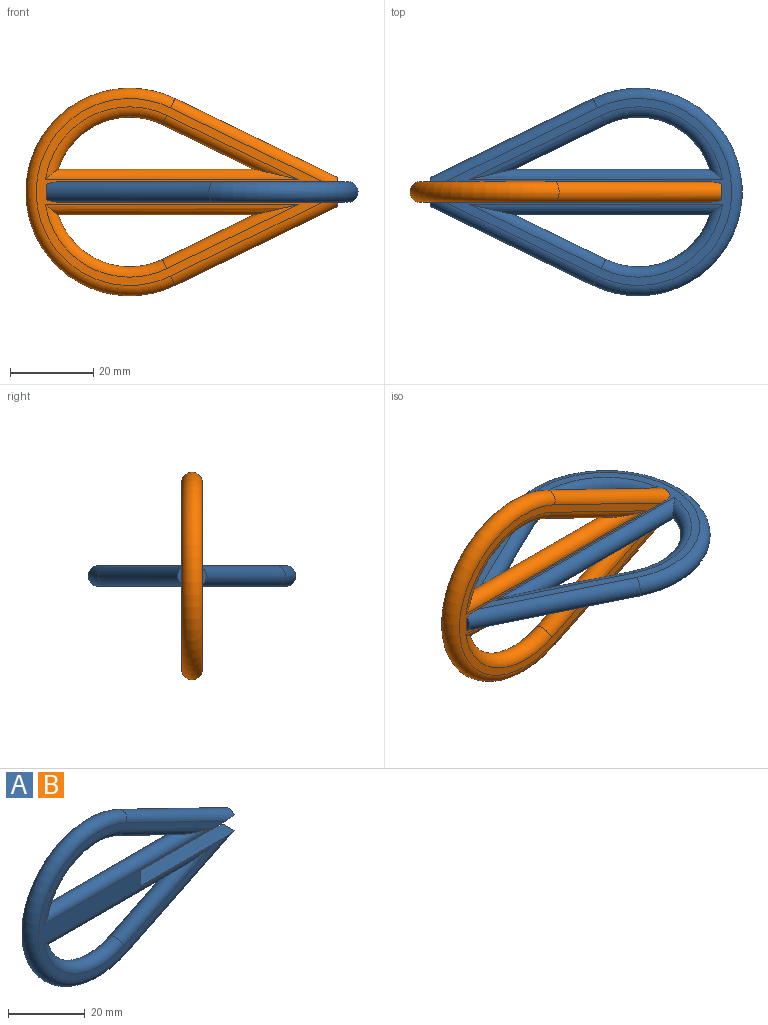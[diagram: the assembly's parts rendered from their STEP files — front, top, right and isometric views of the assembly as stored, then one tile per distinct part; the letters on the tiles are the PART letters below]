
ASSEMBLY  parts=2 mates=1
PART A: 16 faces, bbox 77.5x5x54.1 mm
  f0: plane 35x5mm, normal (0,0,-1), area 173.7mm2, adj f1,f4,f5,f6,f9
  f1: plane 3.84x1mm, normal (1,0,0), area 2.7mm2, adj f0,f9
  f2: plane 3.84x1mm, normal (1,0,0), area 2.7mm2, adj f3,f7
  f3: plane 35x5mm, normal (0,0,1), area 173.7mm2, adj f2,f4,f5,f6,f7
  f4: plane 5x5mm, normal (1,0,0), area 25mm2, adj f0,f3,f5,f6
  f5: plane 68.84x45mm, normal (0,-1,0), area 566.9mm2, adj f0,f3,f4,f7,f8,f9,f10,f11
  f6: plane 68.84x45mm, normal (0,1,0), area 566.9mm2, adj f0,f3,f4,f7,f8,f9,f10,f11
  f7: cylinder r=2.5mm len=40.56mm, axis (-0.9,0,-0.44), area 337.9mm2, adj f2,f3,f5,f6,f8
  f8: torus R=22.5mm, axis (0,-1,0), area 765.6mm2, adj f5,f6,f7,f9
  f9: cylinder r=2.5mm len=40.56mm, axis (0.9,0,-0.44), area 337.9mm2, adj f0,f1,f5,f6,f8
  f10: cylinder r=2.5mm len=61.01mm, axis (-1,0,0), area 409.4mm2, adj f5,f6,f11,f12
  f11: torus R=20.5mm, axis (0,-1,0), area 264mm2, adj f5,f6,f10,f12
  f12: cylinder r=2.5mm len=32.87mm, axis (0.9,0,0.44), area 223.1mm2, adj f5,f6,f10,f11
  f13: cylinder r=2.5mm len=61.01mm, axis (1,0,0), area 409.4mm2, adj f5,f6,f14,f15
  f14: torus R=20.5mm, axis (0,-1,0), area 264mm2, adj f5,f6,f13,f15
  f15: cylinder r=2.5mm len=32.87mm, axis (-0.9,0,0.44), area 223.1mm2, adj f5,f6,f13,f14
PART B: same geometry as A
PLACE A rot(axis=(0,0.71,0.71),180deg) t=(30,-2.5,2.5)mm
PLACE B at identity fixed
MATE fastened A.f4 <-> B.f4  axis (-1,0,0) through (15,-2.5,0)mm
